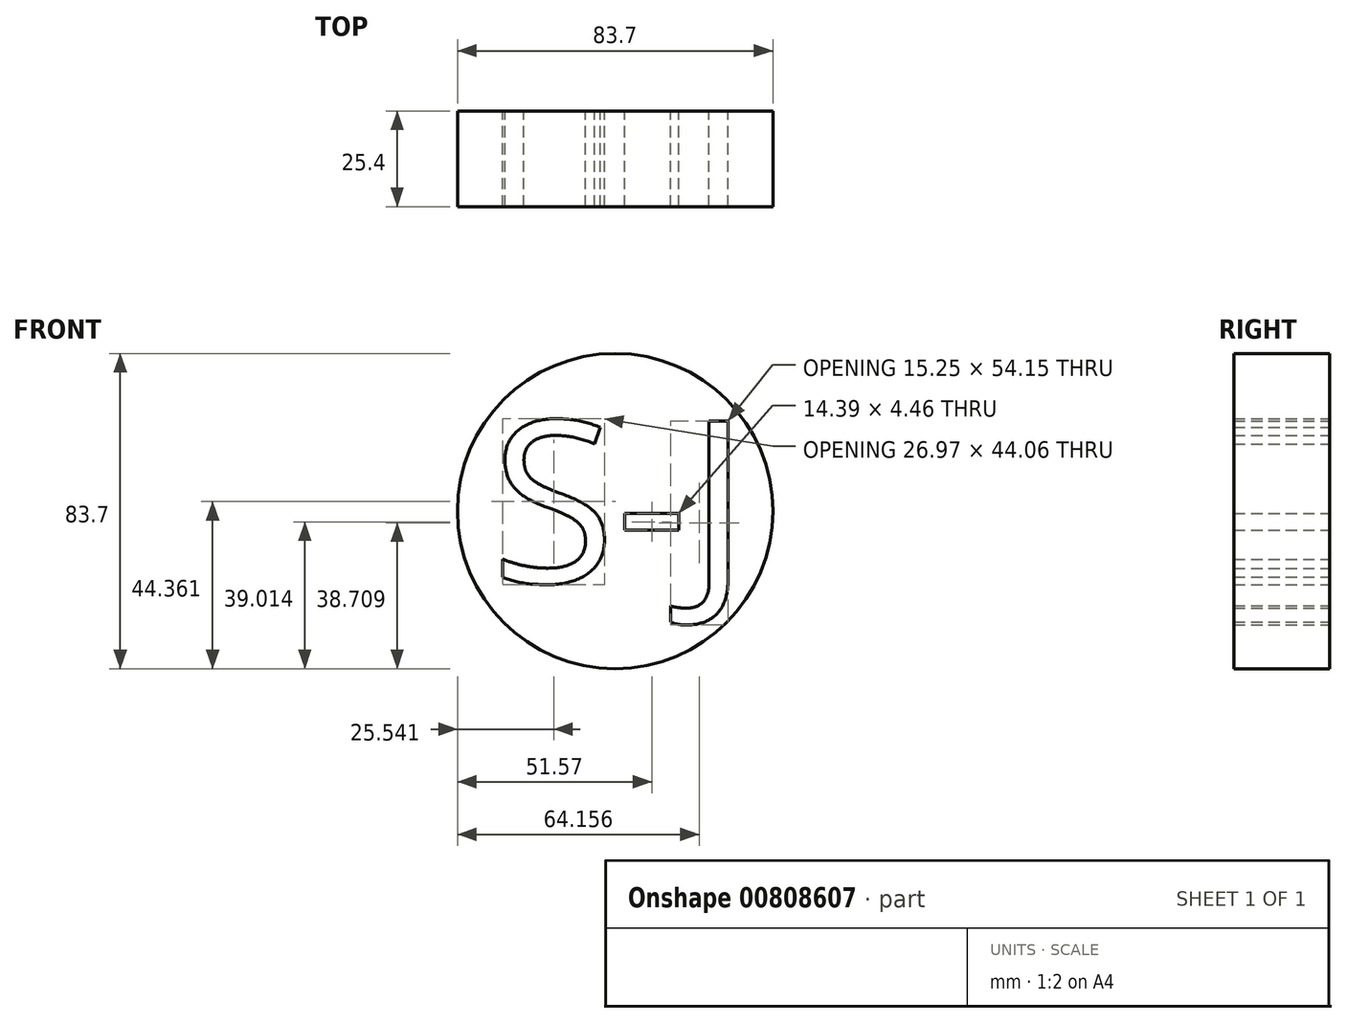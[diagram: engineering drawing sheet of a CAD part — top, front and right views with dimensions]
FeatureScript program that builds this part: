
annotation { "Feature Type Name" : "Feature", "Feature Type Description" : "" }
export const myFeature = defineFeature(function(context is Context, id is Id, definition is map)
    precondition{}
    {
        {
            var Q0;
            Q0=qCreatedBy(makeId("Front.planeOp"),FACE);
            var sketch = newSketch(context, id + "F0", { "sketchPlane" : qUnion([Q0])});
            skCircle(sketch, "E0", {"center": v(0, 0) * mm, "radius": 41.85 * mm});
            skText(sketch, "E1", { "text": "S-J\n", "fontName": "OpenSans-Regular.ttf"});
            const initialGuessF0  = {"E1": [-0.0329, -0.01893, 1, 0, 0.04323]};
            skSetInitialGuess(sketch, initialGuessF0);
            skSolve(sketch);
        }
        {
            var Q0;
            Q0=makeQuery(id+"F0.imprint","IMPRINT",FACE,{"disambiguationData":[TD([[makeQuery(id+"F0.imprint","IMPRINT",EDGE,{"derivedFrom":sQuery(id+"F0.wireOp",EDGE,"E0")}),1.0]])]});
            extrude(context, id + "F1", {"entities" : qUnion([Q0]), "depth" : 25.4 * mm, "offsetDistance" : 25.4 * mm});
        }
    });
